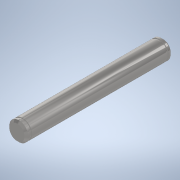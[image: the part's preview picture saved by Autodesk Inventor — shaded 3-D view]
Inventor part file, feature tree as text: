
AUTODESK INVENTOR PART (.ipt)
format: ipt  version: 2022 (Build 260153000, 153)  size: 123,392 bytes
history: native  units: in
note: dims shown in document units (in); Inventor stores cm internally (conversion verified against a paired STEP export)
features: revolve x1, chamfer x1, sketch x1
ambient origin geometry x8: Origin, YZ Plane, XZ Plane, XY Plane, X Axis, Y Axis, Z Axis, Center Point
bodies: Solid1 (feature_tree)
feature tree (3):
  revolve  "Revolution1"  [1 undecoded]
  chamfer  "Chamfer1"  Distance=0.0098in
  sketch  "Sketch1"  dims[d0=0.0984in d1=1.5157in d2=0.0098in d3=0.0197in d4=0.0394in d5=90.0deg d6=0.0197in d7=0.125in d8=45.0deg]
note: 1 required parameter value undecoded (feature->parameter linkage not recoverable at this tier; creation-order binding heuristic only, values carry confidence <= 0.55)
